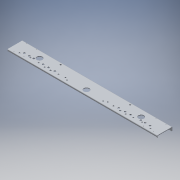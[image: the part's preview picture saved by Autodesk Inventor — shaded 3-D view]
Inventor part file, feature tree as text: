
AUTODESK INVENTOR PART (.ipt)
format: ipt  version: 2017 (Build 210142000, 142)  size: 229,376 bytes
history: native  units: in
note: dims shown in document units (in); Inventor stores cm internally (conversion verified against a paired STEP export)
features: other x4, reference x2, extrude x1, sketch x1
ambient origin geometry x8: Origin, YZ Plane, XZ Plane, XY Plane, X Axis, Y Axis, Z Axis, Center Point
bodies: Solid1 (feature_tree)
feature tree (8):
  extrude  "Extrusion1"  [1 undecoded]
  sketch  "Sketch1"  dims[d0=0.0in d1=0.0in]
  reference  "Reference1"
  reference  "Reference2"
  other  "Cut-Extrude10"
  other  "<userpath>\Documents\Inventor\2017 Robot\Robot Chassis.iam"
  other  "Robot Chassis.iam"
  other  "am-2952a_AM14U3_Inside_Plate:1"
note: 1 required parameter value undecoded (feature->parameter linkage not recoverable at this tier; creation-order binding heuristic only, values carry confidence <= 0.55)
